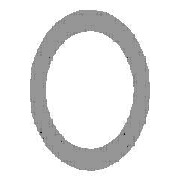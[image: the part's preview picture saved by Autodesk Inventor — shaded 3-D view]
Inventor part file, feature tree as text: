
AUTODESK INVENTOR PART (.ipt)
format: ipt  version: 2013 (Build 170138000, 138)  size: 125,440 bytes
history: native  units: mm (DEFAULTED — no unit token found)
features: plane x8, other x5, sketch x5, extrude x2
ambient origin geometry x8: Origin, YZ Plane, XZ Plane, XY Plane, X Axis, Y Axis, Z Axis, Center Point
bodies: Solid1 (feature_tree), Body (feature_tree)
feature tree (20):
  parser-record x1  (decoder bookkeeping rows leaked as tree rows — omitted from the tree; the rows remain in map.json)
  other  "Driven Length"
  other  "Start plane"
  other  "End plane"
  plane  "Work Plane4"
  plane  "Work Plane5"
  plane  "Work Plane6"
  extrude  "Extrusion2"  Depth=3.556mm
  plane  "Work Plane7"
  plane  "Work Plane8"
  plane  "Work Plane9"
  extrude  "Extrusion3"  TaperAngle=0.0deg  [1 undecoded]
  plane  "Work Plane10"
  sketch  "Sketch"  dims[d7=2143.252mm d8=3.302mm d9=0.0mm d10=3.302mm d11=0.0mm d12=0.0mm]
  sketch  "Sketch3"  dims[d0=42.164mm d1=3.556mm]
  plane  "Work Plane3"
  sketch  "Sketch4"  dims[d2=2143.252mm d3=0.0mm d4=-0.0mm]
  sketch  "Sketch5"  dims[d5=2143.252mm]
  sketch  "Sketch6"  dims[d6=90.0deg]
  other  "Work Axis1"
note: 1 required parameter value undecoded (feature->parameter linkage not recoverable at this tier; creation-order binding heuristic only, values carry confidence <= 0.55)
